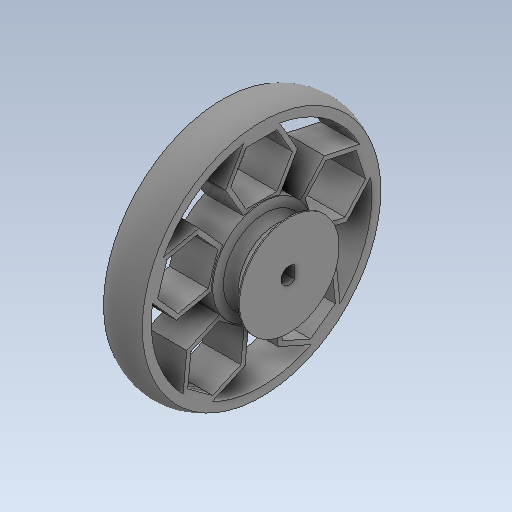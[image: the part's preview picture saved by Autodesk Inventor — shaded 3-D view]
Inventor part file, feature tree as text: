
AUTODESK INVENTOR PART (.ipt)
format: ipt  version: 2020 (Build 240168000, 168)  size: 465,920 bytes
history: native  units: in
note: dims shown in document units (in); Inventor stores cm internally (conversion verified against a paired STEP export)
features: sketch x4, extrude x2, revolve x2, projected_geometry x1
ambient origin geometry x8: Origin, YZ Plane, XZ Plane, XY Plane, X Axis, Y Axis, Z Axis, Center Point
bodies: Solid1 (feature_tree)
feature tree (9):
  extrude  "Extrusion1"  Depth=0.0394in
  sketch  "Sketch3"  dims[d6=0.7087in d7=0.1969in]
  revolve  "Revolution1"  [1 undecoded]
  extrude  "Extrusion2"  Depth=0.1969in
  revolve  "Revolution2"  [1 undecoded]
  sketch  "Sketch1"  dims[d0=0.1181in d1=0.0394in]
  sketch  "Sketch2"  dims[d3=1.6929in d4=0.1181in]
  projected_geometry  "Projected Loop1"
  sketch  "Sketch4"  dims[d8=0.0in d9=1.6929in d10=0.063in d11=0.0315in d16=0.2756in d17=0.0in d19=360.0deg d20=0.0984in d24=0.0394in d25=90.0deg d26=45.0deg d28=0.0079in d29=1.9685in d31=360.0deg]
note: 2 required parameter values undecoded (feature->parameter linkage not recoverable at this tier; creation-order binding heuristic only, values carry confidence <= 0.55)
